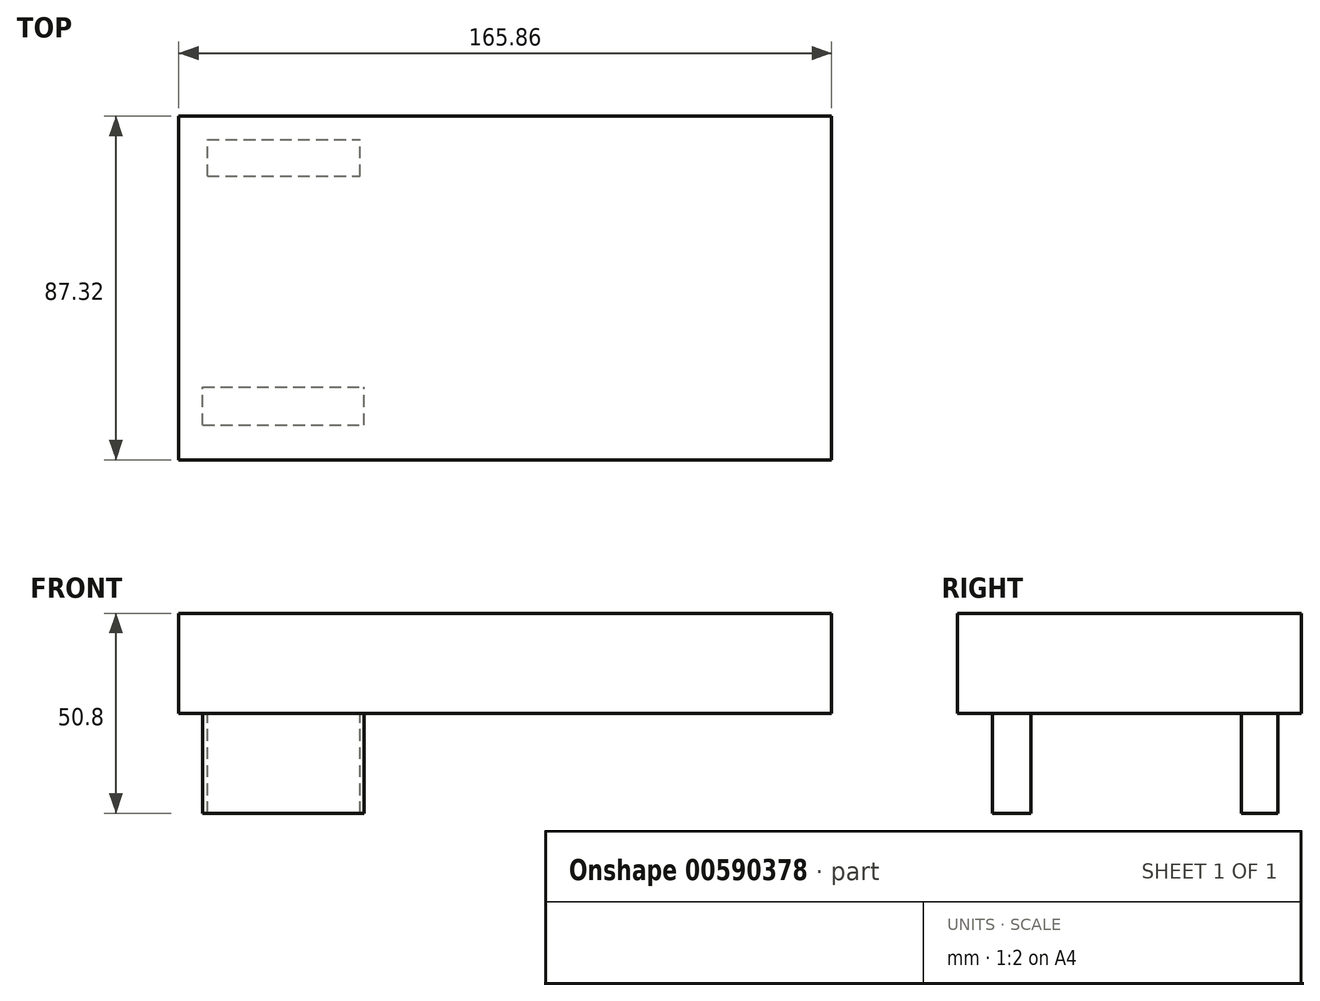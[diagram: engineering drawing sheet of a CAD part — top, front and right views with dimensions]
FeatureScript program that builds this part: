
annotation { "Feature Type Name" : "Feature", "Feature Type Description" : "" }
export const myFeature = defineFeature(function(context is Context, id is Id, definition is map)
    precondition{}
    {
        {
            var Q0;
            Q0=qCreatedBy(makeId("Top.planeOp"),FACE);
            var sketch = newSketch(context, id + "F0", { "sketchPlane" : qUnion([Q0])});
            skLineSegment(sketch, "E0.bottom", {"start": v(-127.2, 34.84) * mm, "end": v(38.67, 34.84) * mm});
            skLineSegment(sketch, "E0.top", {"start": v(-127.2, -52.48) * mm, "end": v(38.67, -52.48) * mm});
            skLineSegment(sketch, "E0.left", {"start": v(-127.2, 34.84) * mm, "end": v(-127.2, -52.48) * mm});
            skLineSegment(sketch, "E0.right", {"start": v(38.67, 34.84) * mm, "end": v(38.67, -52.48) * mm});
            skSolve(sketch);
        }
        {
            var Q0;
            Q0=makeQuery(id+"F0.imprint","IMPRINT",FACE,{"disambiguationData":[TD([[makeQuery(id+"F0.imprint","IMPRINT",EDGE,{"derivedFrom":sQuery(id+"F0.wireOp",EDGE,"E0.bottom")}),-1.0]])]});
            extrude(context, id + "F1", {"entities" : qUnion([Q0]), "depth" : 25.4 * mm, "offsetDistance" : 25.4 * mm});
        }
        {
            var Q0;
            Q0=makeQuery(id+"F1.opExtrude","CAP_FACE",FACE,{"disambiguationData":[OSD([sQuery(id+"F0.wireOp",EDGE,"E0.bottom"),sQuery(id+"F0.wireOp",EDGE,"E0.top"),sQuery(id+"F0.wireOp",EDGE,"E0.left"),sQuery(id+"F0.wireOp",EDGE,"E0.right")])],"isStart":true});
            var sketch = newSketch(context, id + "F2", { "sketchPlane" : qUnion([Q0])});
            skLineSegment(sketch, "E1.bottom", {"start": v(-121.15, 43.65) * mm, "end": v(-80.1, 43.65) * mm});
            skLineSegment(sketch, "E1.top", {"start": v(-121.15, 33.92) * mm, "end": v(-80.1, 33.92) * mm});
            skLineSegment(sketch, "E1.left", {"start": v(-121.15, 43.65) * mm, "end": v(-121.15, 33.92) * mm});
            skLineSegment(sketch, "E1.right", {"start": v(-80.1, 43.65) * mm, "end": v(-80.1, 33.92) * mm});
            skSolve(sketch);
        }
        {
            var Q0;
            Q0=makeQuery(id+"F2.imprint","IMPRINT",FACE,{"disambiguationData":[TD([[makeQuery(id+"F2.imprint","IMPRINT",EDGE,{"derivedFrom":sQuery(id+"F2.wireOp",EDGE,"E1.bottom")}),-1.0]])]});
            extrude(context, id + "F3", {"entities" : qUnion([Q0]), "operationType" : NewBodyOperationType.ADD, "depth" : 25.4 * mm, "offsetDistance" : 25.4 * mm});
        }
        {
            var Q0;
            Q0=makeQuery(id+"F1.opExtrude","CAP_FACE",FACE,{"disambiguationData":[OSD([sQuery(id+"F0.wireOp",EDGE,"E0.bottom"),sQuery(id+"F0.wireOp",EDGE,"E0.top"),sQuery(id+"F0.wireOp",EDGE,"E0.left"),sQuery(id+"F0.wireOp",EDGE,"E0.right")])],"isStart":true});
            var sketch = newSketch(context, id + "F4", { "sketchPlane" : qUnion([Q0])});
            skLineSegment(sketch, "E2.bottom", {"start": v(-119.92, -19.57) * mm, "end": v(-81.16, -19.57) * mm});
            skLineSegment(sketch, "E2.top", {"start": v(-119.92, -28.93) * mm, "end": v(-81.16, -28.93) * mm});
            skLineSegment(sketch, "E2.left", {"start": v(-119.92, -19.57) * mm, "end": v(-119.92, -28.93) * mm});
            skLineSegment(sketch, "E2.right", {"start": v(-81.16, -19.57) * mm, "end": v(-81.16, -28.93) * mm});
            skSolve(sketch);
        }
        {
            var Q0;
            Q0=makeQuery(id+"F4.imprint","IMPRINT",FACE,{"disambiguationData":[TD([[makeQuery(id+"F4.imprint","IMPRINT",EDGE,{"derivedFrom":sQuery(id+"F4.wireOp",EDGE,"E2.bottom")}),-1.0]])]});
            extrude(context, id + "F5", {"entities" : qUnion([Q0]), "operationType" : NewBodyOperationType.ADD, "depth" : 25.4 * mm, "offsetDistance" : 25.4 * mm});
        }
    });
